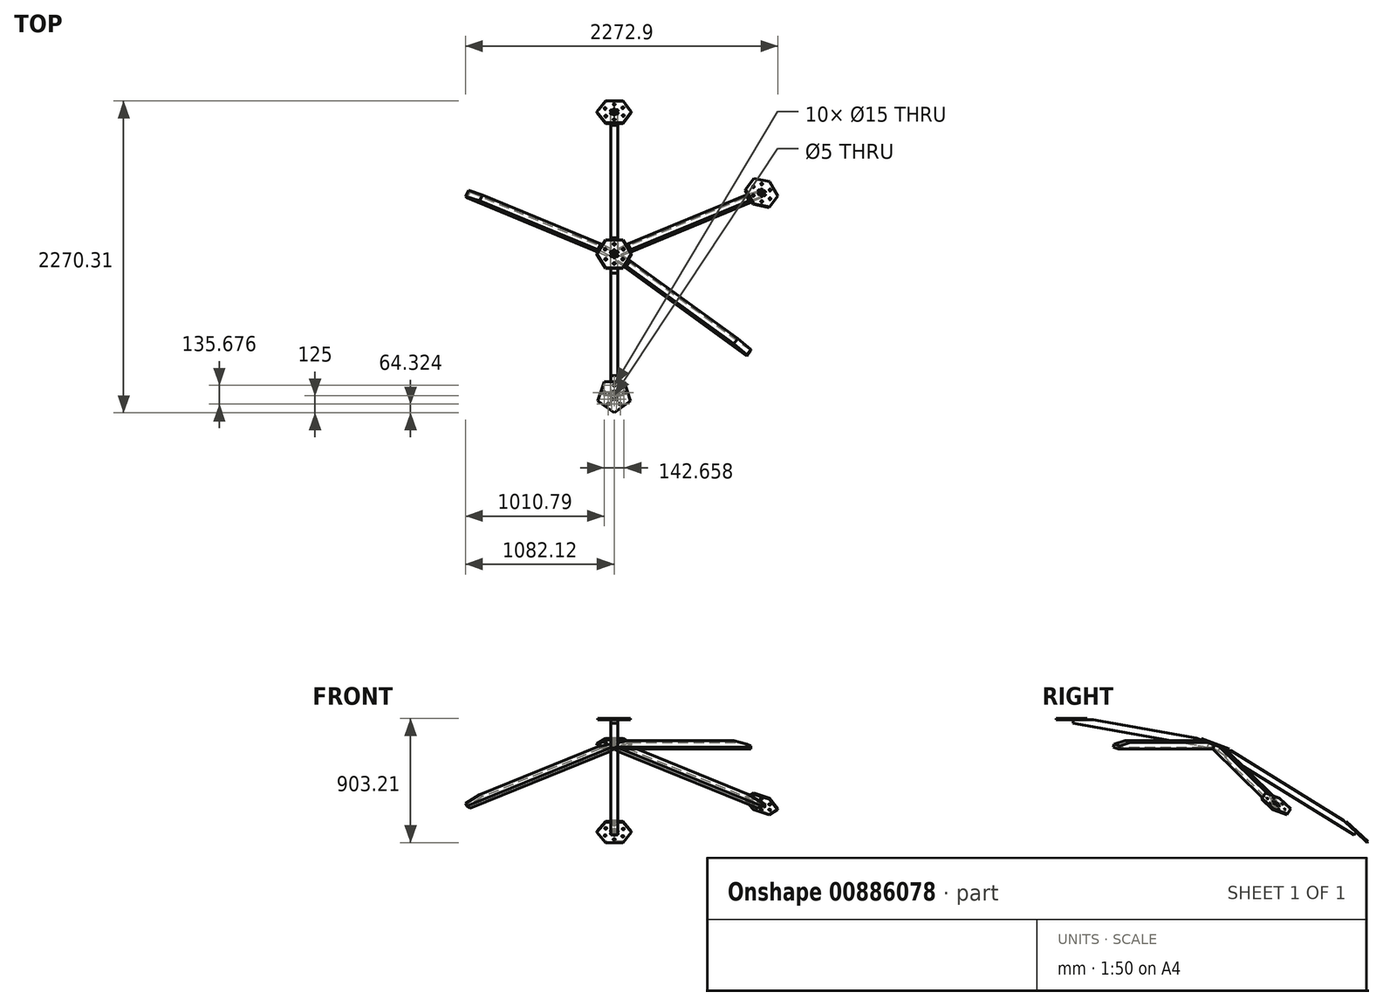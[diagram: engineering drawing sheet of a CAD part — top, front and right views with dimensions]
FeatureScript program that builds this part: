
annotation { "Feature Type Name" : "Feature", "Feature Type Description" : "" }
export const myFeature = defineFeature(function(context is Context, id is Id, definition is map)
    precondition{}
    {
        {
            assignVariable(context, id + "F0", {"name" : "Econnecteur", "anyValue" : 10});
        }
        {
            var Q0;
            Q0=qCreatedBy(makeId("Top.planeOp"),FACE);
            var sketch = newSketch(context, id + "F1", { "sketchPlane" : qUnion([Q0])});
            skLineSegment(sketch, "E0", {"start": v(-73.47, 101.13) * mm, "end": v(73.47, 101.13) * mm});
            skLineSegment(sketch, "E1", {"start": v(73.47, 101.13) * mm, "end": v(118.88, -38.63) * mm});
            skLineSegment(sketch, "E2", {"start": v(118.88, -38.63) * mm, "end": v(0, -125) * mm});
            skLineSegment(sketch, "E3", {"start": v(0, -125) * mm, "end": v(-118.88, -38.63) * mm});
            skLineSegment(sketch, "E4", {"start": v(-118.88, -38.63) * mm, "end": v(-73.47, 101.13) * mm});
            skLineSegment(sketch, "E5", {"start": v(-73.47, 101.13) * mm, "end": v(59.44, -81.81) * mm, "construction": true});
            skLineSegment(sketch, "E6", {"start": v(73.47, 101.13) * mm, "end": v(-59.44, -81.81) * mm, "construction": true});
            skLineSegment(sketch, "E7", {"start": v(118.88, -38.63) * mm, "end": v(-96.18, 31.25) * mm, "construction": true});
            skPoint(sketch, "E7.endSnap0", {"position": v(-96.18, 31.25) * mm});
            skCircle(sketch, "E8", {"center": v(-17.63, -24.27) * mm, "radius": 7.5 * mm});
            skCircle(sketch, "E9", {"center": v(-44.08, -60.68) * mm, "radius": 7.5 * mm});
            skCircle(sketch, "E10", {"center": v(-28.53, 9.27) * mm, "radius": 7.5 * mm});
            skCircle(sketch, "E11", {"center": v(-71.33, 23.18) * mm, "radius": 7.5 * mm});
            skCircle(sketch, "E12", {"center": v(44.08, -60.68) * mm, "radius": 7.5 * mm});
            skCircle(sketch, "E13", {"center": v(17.63, -24.27) * mm, "radius": 7.5 * mm});
            skLineSegment(sketch, "E14", {"start": v(0, 101.13) * mm, "end": v(0, 0) * mm, "construction": true});
            skLineSegment(sketch, "E15", {"start": v(0, 0) * mm, "end": v(96.18, 31.25) * mm, "construction": true});
            skCircle(sketch, "E16", {"center": v(0, 75) * mm, "radius": 7.5 * mm});
            skCircle(sketch, "E17", {"center": v(0, 30) * mm, "radius": 7.5 * mm});
            skCircle(sketch, "E18", {"center": v(71.33, 23.18) * mm, "radius": 7.5 * mm});
            skCircle(sketch, "E19", {"center": v(28.53, 9.27) * mm, "radius": 7.5 * mm});
            skCircle(sketch, "E20", {"center": v(0, 0) * mm, "radius": 75 * mm, "construction": true});
            skCircle(sketch, "E21", {"center": v(0, 0) * mm, "radius": 30 * mm, "construction": true});
            skCircle(sketch, "E22", {"center": v(0, 0) * mm, "radius": 2.5 * mm});
            skCircle(sketch, "E23", {"center": v(0, 0) * mm, "radius": 125 * mm, "construction": true});
            skSolve(sketch);
        }
        {
            var Q0;
            Q0=makeQuery(id+"F1.imprint","IMPRINT",FACE,{"disambiguationData":[TD([[makeQuery(id+"F1.imprint","IMPRINT",EDGE,{"derivedFrom":sQuery(id+"F1.wireOp",EDGE,"E0")}),-1.0]])]});
            extrude(context, id + "F2", {"entities" : qUnion([Q0]), "depth" : (getVariable(context, 'Econnecteur')) * mm, "offsetDistance" : 25 * mm});
        }
        {
            var Q0;
            Q0=qCreatedBy(makeId("Right.planeOp"),FACE);
            var sketch = newSketch(context, id + "F3", { "sketchPlane" : qUnion([Q0])});
            skLineSegment(sketch, "E24", {"start": v(0, 0) * mm, "end": v(145.6, 0) * mm});
            skLineSegment(sketch, "E25", {"start": v(145.6, 0) * mm, "end": v(893.14, -132.35) * mm});
            skLineSegment(sketch, "E26", {"start": v(893.14, -132.35) * mm, "end": v(1029.88, -182.34) * mm});
            skLineSegment(sketch, "E27", {"start": v(0, 0) * mm, "end": v(0, -25) * mm});
            skLineSegment(sketch, "E28", {"start": v(0, -25) * mm, "end": v(1021.3, -205.82) * mm});
            skLineSegment(sketch, "E29", {"start": v(1021.3, -205.82) * mm, "end": v(1029.88, -182.34) * mm});
            skSolve(sketch);
        }
        {
            var Q0;
            Q0=makeQuery(id+"F3.imprint","IMPRINT",FACE,{"disambiguationData":[TD([[makeQuery(id+"F3.imprint","IMPRINT",EDGE,{"derivedFrom":sQuery(id+"F3.wireOp",EDGE,"E24")}),-1.0]])]});
            extrude(context, id + "F4", {"entities" : qUnion([Q0]), "endBound" : BoundingType.SYMMETRIC, "depth" : 50 * mm, "offsetDistance" : 25 * mm});
        }
        {
            var Q0;
            Q0=makeQuery(id+"F4.opExtrude","SWEPT_FACE",FACE,{"disambiguationData":[OSD([sQuery(id+"F3.wireOp",EDGE,"E26")])]});
            var sketch = newSketch(context, id + "F5", { "sketchPlane" : qUnion([Q0])});
            skLineSegment(sketch, "E30", {"start": v(-62.5, 921.63) * mm, "end": v(62.5, 921.63) * mm});
            skLineSegment(sketch, "E31", {"start": v(62.5, 921.63) * mm, "end": v(125, 1029.88) * mm});
            skLineSegment(sketch, "E32", {"start": v(125, 1029.88) * mm, "end": v(62.5, 1138.14) * mm});
            skLineSegment(sketch, "E33", {"start": v(62.5, 1138.14) * mm, "end": v(-62.5, 1138.14) * mm});
            skLineSegment(sketch, "E34", {"start": v(-62.5, 1138.14) * mm, "end": v(-125, 1029.88) * mm});
            skLineSegment(sketch, "E35", {"start": v(-125, 1029.88) * mm, "end": v(-62.5, 921.63) * mm});
            skCircle(sketch, "E36", {"center": v(0, 954.88) * mm, "radius": 7.5 * mm});
            skCircle(sketch, "E37", {"center": v(0, 1004.88) * mm, "radius": 7.5 * mm});
            skCircle(sketch, "E38", {"center": v(0, 1029.88) * mm, "radius": 25 * mm, "construction": true});
            skCircle(sketch, "E39", {"center": v(0, 1029.88) * mm, "radius": 75 * mm, "construction": true});
            skCircle(sketch, "E40", {"center": v(0, 1029.88) * mm, "radius": 2.5 * mm});
            skCircle(sketch, "E41", {"center": v(-61.95, 987.6) * mm, "radius": 7.5 * mm});
            skCircle(sketch, "E42", {"center": v(-20.65, 1015.8) * mm, "radius": 7.5 * mm});
            skCircle(sketch, "E43", {"center": v(-22.1, 1041.56) * mm, "radius": 7.5 * mm});
            skCircle(sketch, "E44", {"center": v(-66.32, 1064.91) * mm, "radius": 7.5 * mm});
            skCircle(sketch, "E45", {"center": v(0, 1104.88) * mm, "radius": 7.5 * mm});
            skCircle(sketch, "E46", {"center": v(66.32, 1064.91) * mm, "radius": 7.5 * mm});
            skCircle(sketch, "E47", {"center": v(61.95, 987.6) * mm, "radius": 7.5 * mm});
            skCircle(sketch, "E48", {"center": v(20.65, 1015.8) * mm, "radius": 7.5 * mm});
            skCircle(sketch, "E49", {"center": v(22.1, 1041.56) * mm, "radius": 7.5 * mm});
            skCircle(sketch, "E50", {"center": v(0, 1054.88) * mm, "radius": 7.5 * mm});
            skCircle(sketch, "E51", {"center": v(0, 1029.88) * mm, "radius": 125 * mm, "construction": true});
            skLineSegment(sketch, "E52", {"start": v(0, 921.63) * mm, "end": v(0, 1029.88) * mm, "construction": true});
            skLineSegment(sketch, "E53", {"start": v(0, 1029.88) * mm, "end": v(89.67, 968.7) * mm, "construction": true});
            skLineSegment(sketch, "E54", {"start": v(0, 1029.88) * mm, "end": v(-89.67, 968.7) * mm, "construction": true});
            skLineSegment(sketch, "E55", {"start": v(0, 1029.88) * mm, "end": v(95.79, 1080.48) * mm, "construction": true});
            skLineSegment(sketch, "E56", {"start": v(0, 1029.88) * mm, "end": v(-95.79, 1080.48) * mm, "construction": true});
            skLineSegment(sketch, "E57", {"start": v(0, 1029.88) * mm, "end": v(0, 1138.14) * mm, "construction": true});
            skSolve(sketch);
        }
        {
            var Q0;
            Q0=qSketchRegion(id+"F5",true);
            extrude(context, id + "F6", {"entities" : qUnion([Q0]), "operationType" : NewBodyOperationType.ADD, "depth" : 10 * mm, "offsetDistance" : 25 * mm});
        }
        {
            var Q0;
            Q0=makeQuery(id+"F6.opExtrude","CAP_FACE",FACE,{"disambiguationData":[OSD([sQuery(id+"F5.wireOp",EDGE,"E30"),sQuery(id+"F5.wireOp",EDGE,"E31"),sQuery(id+"F5.wireOp",EDGE,"E32"),sQuery(id+"F5.wireOp",EDGE,"E33"),sQuery(id+"F5.wireOp",EDGE,"E34"),sQuery(id+"F5.wireOp",EDGE,"E35"),sQuery(id+"F5.wireOp",EDGE,"E36"),sQuery(id+"F5.wireOp",EDGE,"E37"),sQuery(id+"F5.wireOp",EDGE,"E40"),sQuery(id+"F5.wireOp",EDGE,"E41"),sQuery(id+"F5.wireOp",EDGE,"E42"),sQuery(id+"F5.wireOp",EDGE,"E43"),sQuery(id+"F5.wireOp",EDGE,"E44"),sQuery(id+"F5.wireOp",EDGE,"E45"),sQuery(id+"F5.wireOp",EDGE,"E46"),sQuery(id+"F5.wireOp",EDGE,"E47"),sQuery(id+"F5.wireOp",EDGE,"E48"),sQuery(id+"F5.wireOp",EDGE,"E49"),sQuery(id+"F5.wireOp",EDGE,"E50")])],"isStart":false});
            var sketch = newSketch(context, id + "F7", { "sketchPlane" : qUnion([Q0])});
            skLineSegment(sketch, "E58", {"start": v(0, 1029.88) * mm, "end": v(89.67, 968.7) * mm});
            skLineSegment(sketch, "E59", {"start": v(89.67, 968.7) * mm, "end": v(0, 921.63) * mm});
            skLineSegment(sketch, "E60", {"start": v(0, 921.63) * mm, "end": v(0, 1029.88) * mm});
            skLineSegment(sketch, "E61", {"start": v(0, 1029.88) * mm, "end": v(95.79, 1080.48) * mm});
            skLineSegment(sketch, "E62", {"start": v(95.79, 1080.48) * mm, "end": v(89.67, 968.7) * mm});
            skLineSegment(sketch, "E63", {"start": v(0, 1029.88) * mm, "end": v(-89.67, 968.7) * mm});
            skLineSegment(sketch, "E64", {"start": v(-89.67, 968.7) * mm, "end": v(-95.79, 1080.48) * mm});
            skLineSegment(sketch, "E65", {"start": v(-95.79, 1080.48) * mm, "end": v(0, 1138.14) * mm});
            skLineSegment(sketch, "E66", {"start": v(0, 1138.14) * mm, "end": v(95.79, 1080.48) * mm});
            skLineSegment(sketch, "E67", {"start": v(-89.67, 968.7) * mm, "end": v(0, 921.63) * mm});
            skLineSegment(sketch, "E68", {"start": v(-95.79, 1080.48) * mm, "end": v(0, 1029.88) * mm});
            skLineSegment(sketch, "E69", {"start": v(0, 1138.14) * mm, "end": v(0, 1029.88) * mm});
            skSolve(sketch);
        }
        {
            var Q0;
            Q0=sQuery(id+"F7.wireOp",VERTEX,"E58.end");
            var Q1;
            Q1=sQuery(id+"F5.wireOp",VERTEX,"E53.end");
            var Q2;
            Q2=sQuery(id+"F5.wireOp",VERTEX,"E52.end");
            cPlane(context, id + "F8", {"entities" : qUnion([Q0, Q1, Q2]), "cplaneType" : CPlaneType.THREE_POINT, "offset" : 25 * mm, "width" : 150 * mm, "height" : 150 * mm});
        }
        {
            var Q0;
            Q0=qCreatedBy(id+"F8.planeOp",FACE);
            var sketch = newSketch(context, id + "F9", { "sketchPlane" : qUnion([Q0])});
            skLineSegment(sketch, "E70", {"start": v(-580.51, 182.34) * mm, "end": v(-454.06, 182.34) * mm});
            skLineSegment(sketch, "E71", {"start": v(-454.06, 182.34) * mm, "end": v(489.13, -11.96) * mm});
            skLineSegment(sketch, "E72", {"start": v(489.13, -11.96) * mm, "end": v(605.29, -61.94) * mm});
            skLineSegment(sketch, "E73", {"start": v(605.29, -61.94) * mm, "end": v(605.29, -86.94) * mm});
            skLineSegment(sketch, "E74", {"start": v(605.29, -86.94) * mm, "end": v(-580.51, 157.34) * mm});
            skLineSegment(sketch, "E75", {"start": v(-580.51, 157.34) * mm, "end": v(-580.51, 182.34) * mm});
            skSolve(sketch);
        }
        {
            var Q0;
            Q0=makeQuery(id+"F9.imprint","IMPRINT",FACE,{"disambiguationData":[TD([[makeQuery(id+"F9.imprint","IMPRINT",EDGE,{"derivedFrom":sQuery(id+"F9.wireOp",EDGE,"E70")}),-1.0]])]});
            extrude(context, id + "F10", {"entities" : qUnion([Q0]), "operationType" : NewBodyOperationType.ADD, "endBound" : BoundingType.SYMMETRIC, "depth" : 50 * mm, "offsetDistance" : 25 * mm});
        }
        {
            var Q0;
            Q0=qCreatedBy(makeId("Right.planeOp"),FACE);
            var sketch = newSketch(context, id + "F11", { "sketchPlane" : qUnion([Q0])});
            skLineSegment(sketch, "E76", {"start": v(1029.88, -182.34) * mm, "end": v(1021.3, -205.82) * mm});
            skLineSegment(sketch, "E77", {"start": v(1021.3, -205.82) * mm, "end": v(2042.57, -837.06) * mm});
            skLineSegment(sketch, "E78", {"start": v(1967.8, -732.06) * mm, "end": v(1148.65, -225.75) * mm});
            skLineSegment(sketch, "E79", {"start": v(1148.65, -225.75) * mm, "end": v(1029.88, -182.34) * mm});
            skLineSegment(sketch, "E80", {"start": v(1967.8, -732.06) * mm, "end": v(2059.74, -818.89) * mm});
            skLineSegment(sketch, "E81", {"start": v(2059.74, -818.89) * mm, "end": v(2042.57, -837.06) * mm});
            skSolve(sketch);
        }
        {
            var Q0;
            Q0=makeQuery(id+"F11.imprint","IMPRINT",FACE,{"disambiguationData":[TD([[makeQuery(id+"F11.imprint","IMPRINT",EDGE,{"derivedFrom":sQuery(id+"F11.wireOp",EDGE,"E76")}),1.0]])]});
            extrude(context, id + "F12", {"entities" : qUnion([Q0]), "operationType" : NewBodyOperationType.ADD, "endBound" : BoundingType.SYMMETRIC, "depth" : 50 * mm, "offsetDistance" : 25 * mm});
        }
        {
            var Q0;
            Q0=makeQuery(id+"F12.opExtrude","SWEPT_FACE",FACE,{"disambiguationData":[OSD([sQuery(id+"F11.wireOp",EDGE,"E80")])]});
            var sketch = newSketch(context, id + "F13", { "sketchPlane" : qUnion([Q0])});
            skLineSegment(sketch, "E82", {"start": v(-62.5, 1951.52) * mm, "end": v(62.5, 1951.52) * mm});
            skLineSegment(sketch, "E83", {"start": v(62.5, 1951.52) * mm, "end": v(125, 2059.77) * mm});
            skLineSegment(sketch, "E84", {"start": v(125, 2059.77) * mm, "end": v(62.5, 2168.03) * mm});
            skLineSegment(sketch, "E85", {"start": v(62.5, 2168.03) * mm, "end": v(-62.5, 2168.03) * mm});
            skLineSegment(sketch, "E86", {"start": v(-62.5, 2168.03) * mm, "end": v(-125, 2059.77) * mm});
            skLineSegment(sketch, "E87", {"start": v(-125, 2059.77) * mm, "end": v(-62.5, 1951.52) * mm});
            skCircle(sketch, "E88", {"center": v(0, 1984.77) * mm, "radius": 7.5 * mm});
            skCircle(sketch, "E89", {"center": v(0, 2034.77) * mm, "radius": 7.5 * mm});
            skCircle(sketch, "E90", {"center": v(0, 2059.77) * mm, "radius": 25 * mm, "construction": true});
            skCircle(sketch, "E91", {"center": v(0, 2059.77) * mm, "radius": 75 * mm, "construction": true});
            skCircle(sketch, "E92", {"center": v(0, 2059.77) * mm, "radius": 2.5 * mm});
            skCircle(sketch, "E93", {"center": v(-61.95, 2017.5) * mm, "radius": 7.5 * mm});
            skCircle(sketch, "E94", {"center": v(-20.65, 2045.68) * mm, "radius": 7.5 * mm});
            skCircle(sketch, "E95", {"center": v(-22.1, 2071.45) * mm, "radius": 7.5 * mm});
            skCircle(sketch, "E96", {"center": v(-66.32, 2094.8) * mm, "radius": 7.5 * mm});
            skCircle(sketch, "E97", {"center": v(0, 2134.77) * mm, "radius": 7.5 * mm});
            skCircle(sketch, "E98", {"center": v(61.95, 2102.05) * mm, "radius": 7.5 * mm});
            skCircle(sketch, "E99", {"center": v(66.32, 2024.74) * mm, "radius": 7.5 * mm});
            skCircle(sketch, "E100", {"center": v(22.1, 2048.1) * mm, "radius": 7.5 * mm});
            skCircle(sketch, "E101", {"center": v(20.65, 2073.86) * mm, "radius": 7.5 * mm});
            skCircle(sketch, "E102", {"center": v(0, 2084.77) * mm, "radius": 7.5 * mm});
            skCircle(sketch, "E103", {"center": v(0, 2059.77) * mm, "radius": 125 * mm, "construction": true});
            skLineSegment(sketch, "E104", {"start": v(0, 1951.52) * mm, "end": v(0, 2059.77) * mm, "construction": true});
            skLineSegment(sketch, "E105", {"start": v(0, 2059.77) * mm, "end": v(95.79, 2009.17) * mm, "construction": true});
            skLineSegment(sketch, "E106", {"start": v(0, 2059.77) * mm, "end": v(-89.67, 1998.58) * mm, "construction": true});
            skLineSegment(sketch, "E107", {"start": v(0, 2059.77) * mm, "end": v(89.67, 2120.96) * mm, "construction": true});
            skLineSegment(sketch, "E108", {"start": v(0, 2059.77) * mm, "end": v(-95.79, 2110.37) * mm, "construction": true});
            skLineSegment(sketch, "E109", {"start": v(0, 2059.77) * mm, "end": v(0, 2168.03) * mm, "construction": true});
            skSolve(sketch);
        }
        {
            var Q0;
            Q0=qSketchRegion(id+"F13",true);
            extrude(context, id + "F14", {"entities" : qUnion([Q0]), "operationType" : NewBodyOperationType.ADD, "depth" : (getVariable(context, 'Econnecteur')) * mm, "offsetDistance" : 25 * mm});
        }
        {
            var Q0;
            Q0=sQuery(id+"F7.wireOp",VERTEX,"E61.end");
            var Q1;
            Q1=sQuery(id+"F7.wireOp",VERTEX,"E58.start");
            var Q2;
            Q2=sQuery(id+"F5.wireOp",VERTEX,"E55.end");
            cPlane(context, id + "F15", {"entities" : qUnion([Q0, Q1, Q2]), "cplaneType" : CPlaneType.THREE_POINT, "offset" : 25 * mm, "width" : 150 * mm, "height" : 150 * mm});
        }
        {
            var Q0;
            Q0=qCreatedBy(id+"F15.planeOp",FACE);
            var sketch = newSketch(context, id + "F16", { "sketchPlane" : qUnion([Q0])});
            skLineSegment(sketch, "E110", {"start": v(-481.04, 182.34) * mm, "end": v(-604.88, 182.34) * mm});
            skLineSegment(sketch, "E111", {"start": v(-604.88, 182.34) * mm, "end": v(-1578.34, -22.8) * mm});
            skLineSegment(sketch, "E112", {"start": v(-1578.34, -22.8) * mm, "end": v(-1691.65, -72.78) * mm});
            skLineSegment(sketch, "E113", {"start": v(-1691.65, -72.78) * mm, "end": v(-1681.56, -95.65) * mm});
            skLineSegment(sketch, "E114", {"start": v(-1681.56, -95.65) * mm, "end": v(-481.04, 157.34) * mm});
            skLineSegment(sketch, "E115", {"start": v(-481.04, 157.34) * mm, "end": v(-481.04, 182.34) * mm});
            skSolve(sketch);
        }
        {
            var Q0;
            Q0=makeQuery(id+"F16.imprint","IMPRINT",FACE,{"disambiguationData":[TD([[makeQuery(id+"F16.imprint","IMPRINT",EDGE,{"derivedFrom":sQuery(id+"F16.wireOp",EDGE,"E110")}),1.0]])]});
            extrude(context, id + "F17", {"entities" : qUnion([Q0]), "operationType" : NewBodyOperationType.ADD, "endBound" : BoundingType.SYMMETRIC, "depth" : 50 * mm, "offsetDistance" : 25 * mm});
        }
        {
            var Q0;
            Q0=makeQuery(id+"F17.opExtrude","SWEPT_FACE",FACE,{"disambiguationData":[OSD([sQuery(id+"F16.wireOp",EDGE,"E112")])]});
            var sketch = newSketch(context, id + "F18", { "sketchPlane" : qUnion([Q0])});
            skLineSegment(sketch, "E116", {"start": v(848.05, 1468.96) * mm, "end": v(973.05, 1468.96) * mm});
            skLineSegment(sketch, "E117", {"start": v(973.05, 1468.96) * mm, "end": v(1035.55, 1577.21) * mm});
            skLineSegment(sketch, "E118", {"start": v(1035.55, 1577.21) * mm, "end": v(973.05, 1685.46) * mm});
            skLineSegment(sketch, "E119", {"start": v(973.05, 1685.46) * mm, "end": v(848.05, 1685.46) * mm});
            skLineSegment(sketch, "E120", {"start": v(848.05, 1685.46) * mm, "end": v(785.55, 1577.21) * mm});
            skLineSegment(sketch, "E121", {"start": v(785.55, 1577.21) * mm, "end": v(848.05, 1468.96) * mm});
            skCircle(sketch, "E122", {"center": v(910.55, 1502.21) * mm, "radius": 7.5 * mm});
            skCircle(sketch, "E123", {"center": v(910.55, 1552.21) * mm, "radius": 7.5 * mm});
            skCircle(sketch, "E124", {"center": v(910.55, 1577.21) * mm, "radius": 25 * mm, "construction": true});
            skCircle(sketch, "E125", {"center": v(910.55, 1577.21) * mm, "radius": 75 * mm, "construction": true});
            skCircle(sketch, "E126", {"center": v(910.55, 1577.21) * mm, "radius": 2.5 * mm});
            skCircle(sketch, "E127", {"center": v(845.6, 1539.71) * mm, "radius": 7.5 * mm});
            skCircle(sketch, "E128", {"center": v(888.9, 1564.71) * mm, "radius": 7.5 * mm});
            skCircle(sketch, "E129", {"center": v(888.9, 1589.71) * mm, "radius": 7.5 * mm});
            skCircle(sketch, "E130", {"center": v(845.6, 1614.71) * mm, "radius": 7.5 * mm});
            skCircle(sketch, "E131", {"center": v(910.55, 1652.21) * mm, "radius": 7.5 * mm});
            skCircle(sketch, "E132", {"center": v(975.5, 1614.71) * mm, "radius": 7.5 * mm});
            skCircle(sketch, "E133", {"center": v(975.5, 1539.71) * mm, "radius": 7.5 * mm});
            skCircle(sketch, "E134", {"center": v(932.2, 1564.71) * mm, "radius": 7.5 * mm});
            skCircle(sketch, "E135", {"center": v(932.2, 1589.71) * mm, "radius": 7.5 * mm});
            skCircle(sketch, "E136", {"center": v(910.55, 1602.21) * mm, "radius": 7.5 * mm});
            skCircle(sketch, "E137", {"center": v(910.55, 1577.21) * mm, "radius": 125 * mm, "construction": true});
            skLineSegment(sketch, "E138", {"start": v(910.55, 1468.96) * mm, "end": v(910.55, 1577.21) * mm, "construction": true});
            skLineSegment(sketch, "E139", {"start": v(910.55, 1577.21) * mm, "end": v(1004.3, 1523.08) * mm, "construction": true});
            skLineSegment(sketch, "E140", {"start": v(910.55, 1577.21) * mm, "end": v(816.8, 1523.08) * mm, "construction": true});
            skLineSegment(sketch, "E141", {"start": v(910.55, 1577.21) * mm, "end": v(1004.3, 1631.34) * mm, "construction": true});
            skLineSegment(sketch, "E142", {"start": v(910.55, 1577.21) * mm, "end": v(816.8, 1631.34) * mm, "construction": true});
            skLineSegment(sketch, "E143", {"start": v(910.55, 1577.21) * mm, "end": v(910.55, 1685.46) * mm, "construction": true});
            skSolve(sketch);
        }
        {
            var Q0;
            Q0=qSketchRegion(id+"F18",true);
            extrude(context, id + "F19", {"entities" : qUnion([Q0]), "depth" : (getVariable(context, 'Econnecteur')) * mm, "offsetDistance" : 25 * mm});
        }
        {
            var Q0;
            Q0=sQuery(id+"F5.wireOp",VERTEX,"E56.end");
            var Q1;
            Q1=sQuery(id+"F5.wireOp",VERTEX,"E52.end");
            var Q2;
            Q2=sQuery(id+"F7.wireOp",VERTEX,"E64.end");
            cPlane(context, id + "F20", {"entities" : qUnion([Q0, Q1, Q2]), "cplaneType" : CPlaneType.THREE_POINT, "offset" : 25 * mm, "width" : 150 * mm, "height" : 150 * mm});
        }
        {
            var Q0;
            Q0=qCreatedBy(id+"F20.planeOp",FACE);
            var sketch = newSketch(context, id + "F21", { "sketchPlane" : qUnion([Q0])});
            skLineSegment(sketch, "E144", {"start": v(481.04, 182.34) * mm, "end": v(604.88, 182.34) * mm});
            skLineSegment(sketch, "E145", {"start": v(604.88, 182.34) * mm, "end": v(1578.34, -22.8) * mm});
            skLineSegment(sketch, "E146", {"start": v(1578.34, -22.8) * mm, "end": v(1691.65, -72.78) * mm});
            skLineSegment(sketch, "E147", {"start": v(1691.65, -72.78) * mm, "end": v(1681.56, -95.65) * mm});
            skLineSegment(sketch, "E148", {"start": v(1681.56, -95.65) * mm, "end": v(481.04, 157.34) * mm});
            skLineSegment(sketch, "E149", {"start": v(481.04, 157.34) * mm, "end": v(481.04, 182.34) * mm});
            skSolve(sketch);
        }
        {
            var Q0;
            Q0=makeQuery(id+"F21.imprint","IMPRINT",FACE,{"disambiguationData":[TD([[makeQuery(id+"F21.imprint","IMPRINT",EDGE,{"derivedFrom":sQuery(id+"F21.wireOp",EDGE,"E144")}),-1.0]])]});
            extrude(context, id + "F22", {"entities" : qUnion([Q0]), "operationType" : NewBodyOperationType.ADD, "endBound" : BoundingType.SYMMETRIC, "depth" : 50 * mm, "offsetDistance" : 25 * mm});
        }
    });
